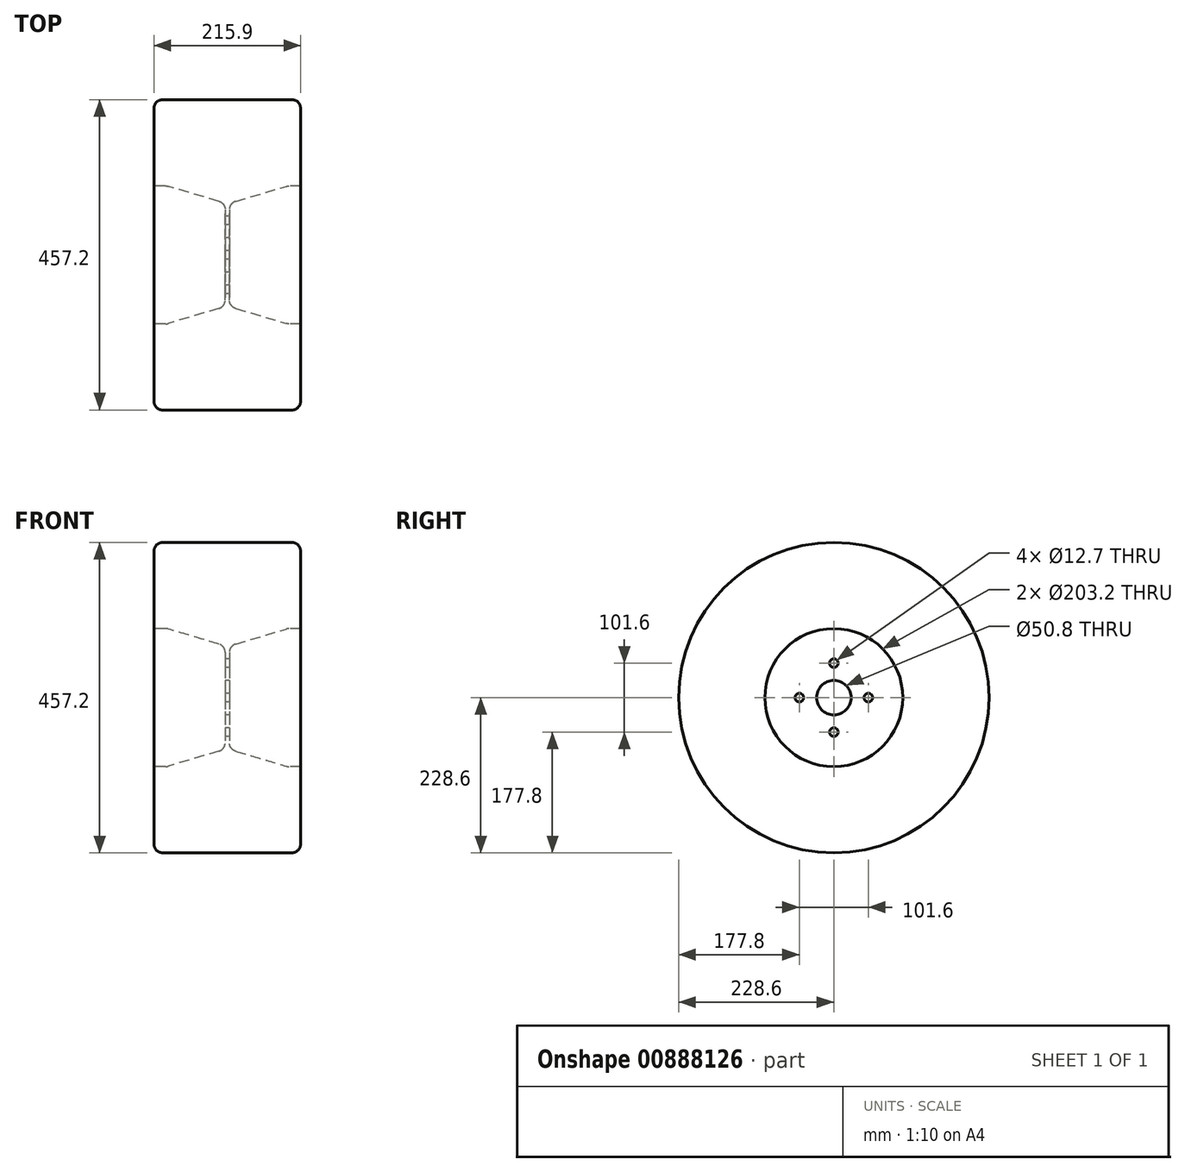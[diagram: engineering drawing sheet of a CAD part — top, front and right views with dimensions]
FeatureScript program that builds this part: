
annotation { "Feature Type Name" : "Feature", "Feature Type Description" : "" }
export const myFeature = defineFeature(function(context is Context, id is Id, definition is map)
    precondition{}
    {
        {
            var Q0;
            Q0=qCreatedBy(makeId("Front.planeOp"),FACE);
            var sketch = newSketch(context, id + "F0", { "sketchPlane" : qUnion([Q0])});
            skLineSegment(sketch, "E0", {"start": v(0, 0) * mm, "end": v(0, 25.4) * mm, "construction": true});
            skLineSegment(sketch, "E1", {"start": v(0, 25.4) * mm, "end": v(3.18, 25.4) * mm});
            skLineSegment(sketch, "E2", {"start": v(3.18, 25.4) * mm, "end": v(3.18, 76.2) * mm});
            skLineSegment(sketch, "E3", {"start": v(3.17, 76.2) * mm, "end": v(88.9, 101.6) * mm});
            skLineSegment(sketch, "E4", {"start": v(107.95, 228.6) * mm, "end": v(0, 228.6) * mm});
            skLineSegment(sketch, "E5.MirrorCS", {"start": v(0, 25.4) * mm, "end": v(-3.18, 25.4) * mm});
            skLineSegment(sketch, "E6.MirrorCS", {"start": v(-3.18, 25.4) * mm, "end": v(-3.18, 76.2) * mm});
            skLineSegment(sketch, "E7.MirrorCS", {"start": v(-3.17, 76.2) * mm, "end": v(-88.9, 101.6) * mm});
            skLineSegment(sketch, "E8.MirrorCS", {"start": v(-107.95, 228.6) * mm, "end": v(0, 228.6) * mm});
            skLineSegment(sketch, "E9", {"start": v(0, 0) * mm, "end": v(3.18, 0) * mm, "construction": true});
            skLineSegment(sketch, "E10", {"start": v(88.9, 101.6) * mm, "end": v(107.95, 101.6) * mm});
            skLineSegment(sketch, "E11", {"start": v(107.95, 101.6) * mm, "end": v(107.95, 228.6) * mm});
            skLineSegment(sketch, "E12", {"start": v(-88.9, 101.6) * mm, "end": v(-107.95, 101.6) * mm});
            skLineSegment(sketch, "E13", {"start": v(-107.95, 101.6) * mm, "end": v(-107.95, 228.6) * mm});
            skSolve(sketch);
        }
        {
            var Q0;
            Q0 = qSketchRegion(id + "F0", true);
            var Q1;
            Q1=sQuery(id+"F0.wireOp",EDGE,"E9");
            revolve(context, id + "F1", {"surfaceOperationType" : NewSurfaceOperationType.NEW, "entities" : qUnion([Q0]), "axis" : qUnion([Q1]), "revolveType" : RevolveType.FULL});
        }
        {
            var Q0;
            Q0=makeQuery(id+"F1.opRevolve","SWEPT_FACE",FACE,{"disambiguationData":[OSD([sQuery(id+"F0.wireOp",EDGE,"E4"),sQuery(id+"F0.wireOp",EDGE,"E8.MirrorCS")])]});
            var Q1;
            Q1=makeQuery(id+"F1.opRevolve","SWEPT_FACE",FACE,{"disambiguationData":[OSD([sQuery(id+"F0.wireOp",EDGE,"E3")])]});
            var Q2;
            Q2=makeQuery(id+"F1.opRevolve","SWEPT_FACE",FACE,{"disambiguationData":[OSD([sQuery(id+"F0.wireOp",EDGE,"E7.MirrorCS")])]});
            fillet(context, id + "F2", {"entities" : qUnion([Q0, Q1, Q2]), "radius" : 12.7 * mm, "tangentPropagation" : true, "allowEdgeOverflow" : false});
        }
        {
            var Q0;
            Q0=qCreatedBy(makeId("Right.planeOp"),FACE);
            var sketch = newSketch(context, id + "F3", { "sketchPlane" : qUnion([Q0])});
            skLineSegment(sketch, "E14", {"start": v(0, 0) * mm, "end": v(0, 50.8) * mm, "construction": true});
            skCircle(sketch, "E15", {"center": v(0, 50.8) * mm, "radius": 6.35 * mm});
            skCircle(sketch, "E16.1.0", {"center": v(-50.8, 0) * mm, "radius": 6.35 * mm});
            skCircle(sketch, "E16.2.0", {"center": v(0, -50.8) * mm, "radius": 6.35 * mm});
            skCircle(sketch, "E16.3.0", {"center": v(50.8, 0) * mm, "radius": 6.35 * mm});
            skPoint(sketch, "E16.center", {"position": v(0, 0) * mm});
            skSolve(sketch);
        }
        {
            var Q0;
            Q0 = qSketchRegion(id + "F3", true);
            extrude(context, id + "F4", {"entities" : qUnion([Q0]), "operationType" : NewBodyOperationType.REMOVE, "endBound" : BoundingType.THROUGH_ALL, "depth" : 25.4 * mm, "offsetDistance" : 25.4 * mm, "hasSecondDirection" : true, "secondDirectionBound" : BoundingType.THROUGH_ALL, "secondDirectionOppositeDirection" : true, "secondDirectionDepth" : 25.4 * mm});
        }
    });
